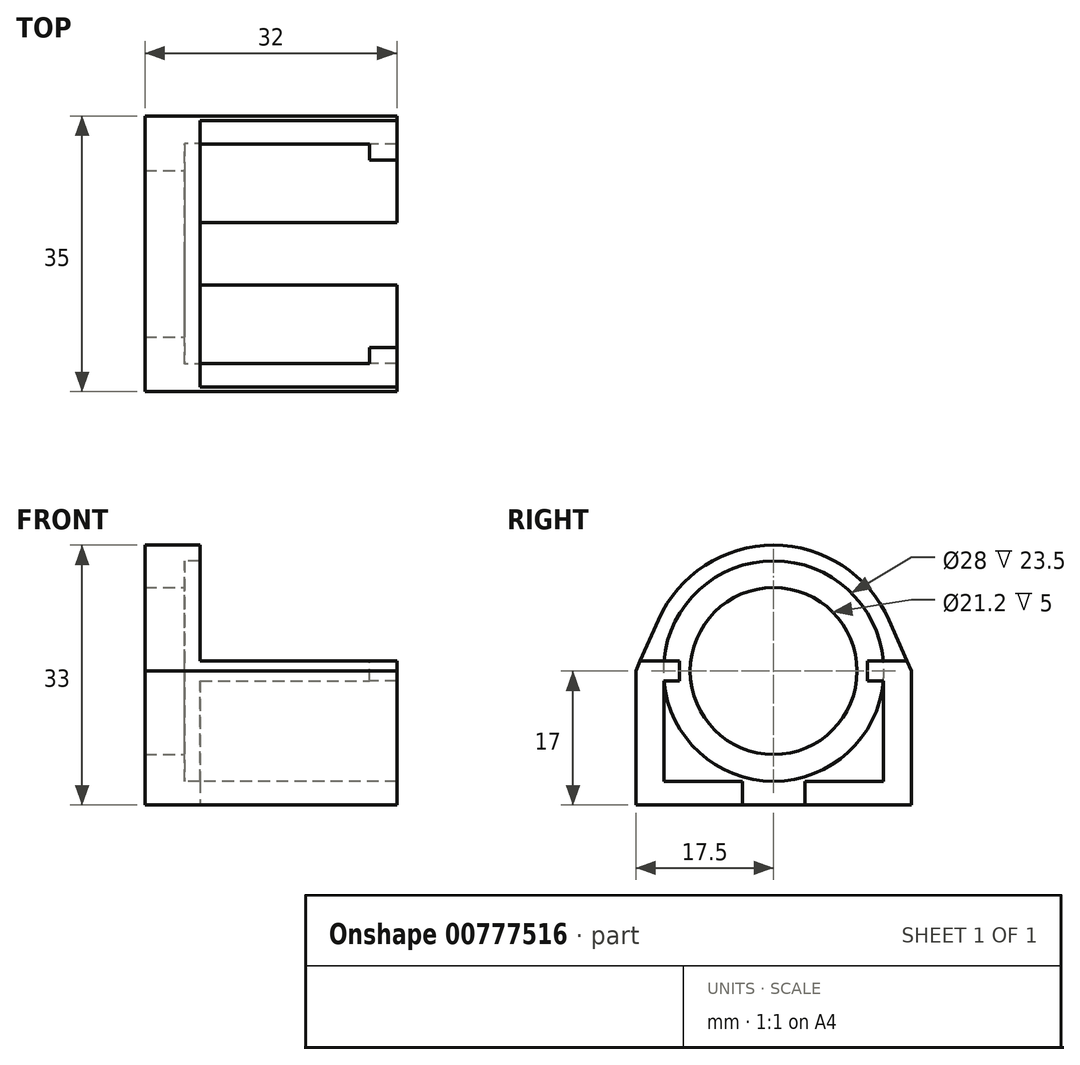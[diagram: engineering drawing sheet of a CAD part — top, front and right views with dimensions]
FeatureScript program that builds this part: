
annotation { "Feature Type Name" : "Feature", "Feature Type Description" : "" }
export const myFeature = defineFeature(function(context is Context, id is Id, definition is map)
    precondition{}
    {
        {
            var Q0;
            Q0=qCreatedBy(makeId("Right.planeOp"),FACE);
            var sketch = newSketch(context, id + "F0", { "sketchPlane" : qUnion([Q0])});
            skCircle(sketch, "E0", {"center": v(0, 0) * mm, "radius": 14 * mm});
            skLineSegment(sketch, "E1", {"start": v(-17.5, -17) * mm, "end": v(-17.5, 0) * mm});
            skLineSegment(sketch, "E2", {"start": v(-17.5, 0) * mm, "end": v(-14.63, 6.48) * mm});
            skLineSegment(sketch, "E3", {"start": v(0, 39.5) * mm, "end": v(0, -17) * mm, "construction": true});
            skLineSegment(sketch, "E4", {"start": v(0, -17) * mm, "end": v(-17.5, -17) * mm});
            skLineSegment(sketch, "E5.MirrorCS", {"start": v(0, -17) * mm, "end": v(17.5, -17) * mm});
            skLineSegment(sketch, "E6.MirrorCS", {"start": v(17.5, 0) * mm, "end": v(14.63, 6.48) * mm});
            skLineSegment(sketch, "E7.MirrorCS", {"start": v(17.5, -17) * mm, "end": v(17.5, 0) * mm});
            skPoint(sketch, "E8.visualSharp", {"position": v(0, 39.5) * mm});
            skArc(sketch, "E8.filletArc", {"start": v(14.63, 6.48) * mm, "mid": v(0, 16) * mm, "end": v(-14.63, 6.48) * mm});
            skSolve(sketch);
        }
        {
            var Q0;
            Q0=makeQuery(id+"F0.imprint","IMPRINT",FACE,{"disambiguationData":[TD([[makeQuery(id+"F0.imprint","IMPRINT",EDGE,{"derivedFrom":sQuery(id+"F0.wireOp",EDGE,"E0")}),-1.0]])]});
            extrude(context, id + "F1", {"entities" : qUnion([Q0]), "depth" : 2 * mm, "offsetDistance" : 25.4 * mm});
        }
        {
            var Q0;
            Q0=makeQuery(id+"F1.opExtrude","CAP_FACE",FACE,{"disambiguationData":[OSD([sQuery(id+"F0.wireOp",EDGE,"E0"),sQuery(id+"F0.wireOp",EDGE,"E1"),sQuery(id+"F0.wireOp",EDGE,"E2"),sQuery(id+"F0.wireOp",EDGE,"E4"),sQuery(id+"F0.wireOp",EDGE,"E5.MirrorCS"),sQuery(id+"F0.wireOp",EDGE,"E6.MirrorCS"),sQuery(id+"F0.wireOp",EDGE,"E7.MirrorCS"),sQuery(id+"F0.wireOp",EDGE,"E8.filletArc")])],"isStart":false});
            var sketch = newSketch(context, id + "F2", { "sketchPlane" : qUnion([Q0])});
            skLineSegment(sketch, "E9", {"start": v(0, 1.25) * mm, "end": v(-11.93, 1.25) * mm, "construction": true});
            skLineSegment(sketch, "E10", {"start": v(-11.93, 1.25) * mm, "end": v(-16.95, 1.25) * mm});
            skLineSegment(sketch, "E11", {"start": v(-16.95, 1.25) * mm, "end": v(-17.5, 0) * mm});
            skLineSegment(sketch, "E12", {"start": v(-17.5, 0) * mm, "end": v(-17.5, -17) * mm});
            skLineSegment(sketch, "E13", {"start": v(-17.5, -17) * mm, "end": v(-13.94, -17) * mm});
            skLineSegment(sketch, "E14", {"start": v(-13.94, -17) * mm, "end": v(-13.94, -1.25) * mm});
            skLineSegment(sketch, "E15", {"start": v(-13.94, -1.25) * mm, "end": v(-11.93, -1.25) * mm});
            skLineSegment(sketch, "E16", {"start": v(-11.93, -1.25) * mm, "end": v(-11.93, 1.25) * mm});
            skLineSegment(sketch, "E17", {"start": v(0, 0) * mm, "end": v(0, -17) * mm, "construction": true});
            skLineSegment(sketch, "E18.MirrorCS", {"start": v(11.93, -1.25) * mm, "end": v(11.93, 1.25) * mm});
            skLineSegment(sketch, "E19.MirrorCS", {"start": v(13.94, -1.25) * mm, "end": v(11.93, -1.25) * mm});
            skLineSegment(sketch, "E20.MirrorCS", {"start": v(16.95, 1.25) * mm, "end": v(17.5, 0) * mm});
            skLineSegment(sketch, "E21.MirrorCS", {"start": v(17.5, -17) * mm, "end": v(13.94, -17) * mm});
            skLineSegment(sketch, "E22.MirrorCS", {"start": v(17.5, 0) * mm, "end": v(17.5, -17) * mm});
            skLineSegment(sketch, "E23.MirrorCS", {"start": v(11.93, 1.25) * mm, "end": v(16.95, 1.25) * mm});
            skLineSegment(sketch, "E24.MirrorCS", {"start": v(13.94, -17) * mm, "end": v(13.94, -1.25) * mm});
            skSolve(sketch);
        }
        {
            var Q0;
            Q0 = qSketchRegion(id + "F2", true);
            extrude(context, id + "F3", {"entities" : qUnion([Q0]), "operationType" : NewBodyOperationType.ADD, "depth" : 25 * mm, "offsetDistance" : 25.4 * mm});
        }
        {
            var Q0;
            Q0=qCreatedBy(makeId("Right.planeOp"),FACE);
            var sketch = newSketch(context, id + "F4", { "sketchPlane" : qUnion([Q0])});
            skLineSegment(sketch, "E25.0.0", {"start": v(17.5, -17) * mm, "end": v(17.5, 0) * mm});
            skLineSegment(sketch, "E25.0.1", {"start": v(17.5, 0) * mm, "end": v(14.63, 6.48) * mm});
            skArc(sketch, "E25.0.2", {"start": v(14.63, 6.48) * mm, "mid": v(0, 16) * mm, "end": v(-14.63, 6.48) * mm});
            skLineSegment(sketch, "E25.0.3", {"start": v(-14.63, 6.48) * mm, "end": v(-17.5, 0) * mm});
            skLineSegment(sketch, "E25.0.4", {"start": v(-17.5, 0) * mm, "end": v(-17.5, -17) * mm});
            skLineSegment(sketch, "E25.0.5", {"start": v(-17.5, -17) * mm, "end": v(0, -17) * mm});
            skLineSegment(sketch, "E25.0.6", {"start": v(0, -17) * mm, "end": v(17.5, -17) * mm});
            skCircle(sketch, "E26", {"center": v(0, 0) * mm, "radius": 10.6 * mm});
            skSolve(sketch);
        }
        {
            var Q0;
            Q0=makeQuery(id+"F4.imprint","IMPRINT",FACE,{"disambiguationData":[TD([[makeQuery(id+"F4.imprint","IMPRINT",EDGE,{"derivedFrom":sQuery(id+"F4.wireOp",EDGE,"E25.0.0")}),1.0]])]});
            extrude(context, id + "F5", {"entities" : qUnion([Q0]), "operationType" : NewBodyOperationType.ADD, "oppositeDirection" : true, "depth" : 5 * mm, "offsetDistance" : 25.4 * mm});
        }
        {
            var Q0;
            Q0=makeQuery(id+"F0.imprint","IMPRINT",FACE,{"disambiguationData":[TD([[makeQuery(id+"F0.imprint","IMPRINT",EDGE,{"derivedFrom":sQuery(id+"F0.wireOp",EDGE,"E0")}),1.0]])]});
            cPlane(context, id + "F6", {"entities" : qUnion([Q0]), "cplaneType" : CPlaneType.OFFSET, "offset" : 23.5 * mm, "width" : 152.4 * mm, "height" : 152.4 * mm});
        }
        {
            var Q0;
            Q0=qCreatedBy(id+"F6.planeOp",FACE);
            var sketch = newSketch(context, id + "F7", { "sketchPlane" : qUnion([Q0])});
            skCircle(sketch, "E27", {"center": v(0, 0) * mm, "radius": 14 * mm});
            skSolve(sketch);
        }
        {
            var Q0;
            Q0=makeQuery(id+"F7.imprint","IMPRINT",FACE,{"disambiguationData":[TD([[makeQuery(id+"F7.imprint","IMPRINT",EDGE,{"derivedFrom":sQuery(id+"F7.wireOp",EDGE,"E27")}),1.0]])]});
            extrude(context, id + "F8", {"entities" : qUnion([Q0]), "operationType" : NewBodyOperationType.REMOVE, "oppositeDirection" : true, "depth" : 23.5 * mm, "offsetDistance" : 25.4 * mm});
        }
        {
            var Q0;
            Q0=qCreatedBy(makeId("Right.planeOp"),FACE);
            var sketch = newSketch(context, id + "F9", { "sketchPlane" : qUnion([Q0])});
            skLineSegment(sketch, "E28.bottom", {"start": v(-3.94, -17) * mm, "end": v(-13.94, -17) * mm});
            skLineSegment(sketch, "E28.top", {"start": v(-3.94, -14) * mm, "end": v(-13.94, -14) * mm});
            skLineSegment(sketch, "E28.left", {"start": v(-3.94, -17) * mm, "end": v(-3.94, -14) * mm});
            skLineSegment(sketch, "E28.right", {"start": v(-13.94, -17) * mm, "end": v(-13.94, -14) * mm});
            skLineSegment(sketch, "E29", {"start": v(0, 0) * mm, "end": v(0, -18.4) * mm, "construction": true});
            skLineSegment(sketch, "E30.MirrorCS", {"start": v(3.94, -17) * mm, "end": v(13.94, -17) * mm});
            skLineSegment(sketch, "E31.MirrorCS", {"start": v(13.94, -17) * mm, "end": v(13.94, -14) * mm});
            skLineSegment(sketch, "E32.MirrorCS", {"start": v(3.94, -14) * mm, "end": v(13.94, -14) * mm});
            skLineSegment(sketch, "E33.MirrorCS", {"start": v(3.94, -17) * mm, "end": v(3.94, -14) * mm});
            skSolve(sketch);
        }
        {
            var Q0;
            Q0 = qSketchRegion(id + "F9", true);
            extrude(context, id + "F10", {"entities" : qUnion([Q0]), "operationType" : NewBodyOperationType.ADD, "depth" : 27 * mm, "offsetDistance" : 25.4 * mm});
        }
        {
            var Q0;
            Q0 = qSketchRegion(id + "F9", true);
            extrude(context, id + "F11", {"entities" : qUnion([Q0]), "operationType" : NewBodyOperationType.ADD, "oppositeDirection" : true, "depth" : 5 * mm, "offsetDistance" : 25.4 * mm});
        }
    });
